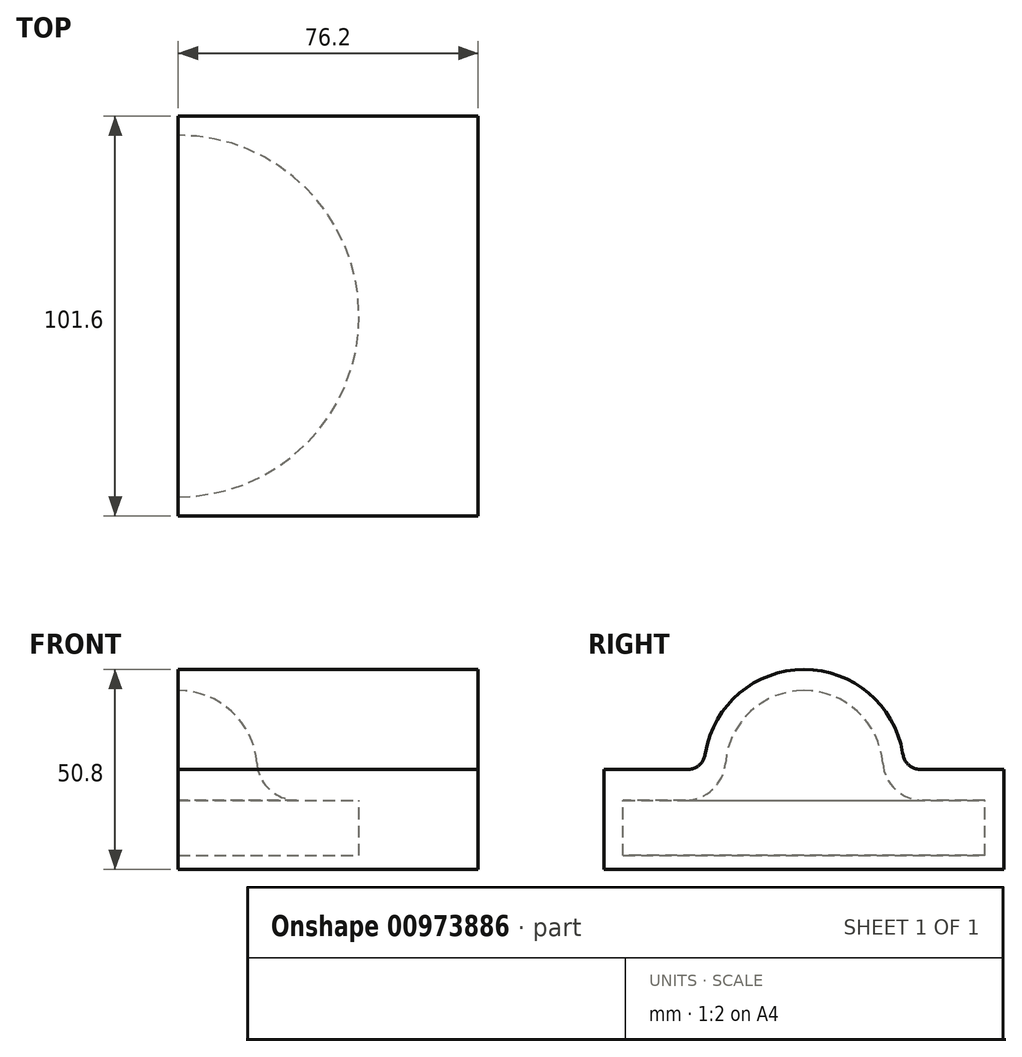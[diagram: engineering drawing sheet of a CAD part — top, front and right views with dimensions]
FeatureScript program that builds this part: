
annotation { "Feature Type Name" : "Feature", "Feature Type Description" : "" }
export const myFeature = defineFeature(function(context is Context, id is Id, definition is map)
    precondition{}
    {
        {
            var Q0;
            Q0=qCreatedBy(makeId("Right.planeOp"),FACE);
            var sketch = newSketch(context, id + "F0", { "sketchPlane" : qUnion([Q0])});
            skLineSegment(sketch, "E0.bottom", {"start": v(0, 0) * mm, "end": v(50.8, 0) * mm});
            skLineSegment(sketch, "E0.top", {"start": v(25.4, 25.4) * mm, "end": v(50.8, 25.4) * mm});
            skLineSegment(sketch, "E0.left", {"start": v(0, 0) * mm, "end": v(0, 25.4) * mm, "construction": true});
            skLineSegment(sketch, "E0.right", {"start": v(50.8, 0) * mm, "end": v(50.8, 25.4) * mm});
            skLineSegment(sketch, "E1.MirrorCS", {"start": v(-25.4, 25.4) * mm, "end": v(-50.8, 25.4) * mm});
            skLineSegment(sketch, "E2.MirrorCS", {"start": v(-50.8, 0) * mm, "end": v(-50.8, 25.4) * mm});
            skLineSegment(sketch, "E3.MirrorCS", {"start": v(0, 0) * mm, "end": v(-50.8, 0) * mm});
            skArc(sketch, "E4", {"start": v(-25.4, 25.4) * mm, "mid": v(0, 50.8) * mm, "end": v(25.4, 25.4) * mm});
            skLineSegment(sketch, "E5", {"start": v(0, 50.8) * mm, "end": v(0, 25.4) * mm, "construction": true});
            skSolve(sketch);
        }
        {
            var Q0;
            Q0=makeQuery(id+"F0.imprint","IMPRINT",FACE,{"disambiguationData":[TD([[makeQuery(id+"F0.imprint","IMPRINT",EDGE,{"derivedFrom":sQuery(id+"F0.wireOp",EDGE,"E0.bottom")}),1.0]])]});
            extrude(context, id + "F1", {"entities" : qUnion([Q0]), "depth" : 76.2 * mm, "offsetDistance" : 25.4 * mm});
        }
        {
            var Q0;
            Q0=makeQuery(id+"F1.opExtrude","SWEPT_EDGE",EDGE,{"disambiguationData":[OSD([sQuery(id+"F0.wireOp",EDGE,"E1.MirrorCS"),sQuery(id+"F0.wireOp",EDGE,"E4")])]});
            var Q1;
            Q1=makeQuery(id+"F1.opExtrude","SWEPT_EDGE",EDGE,{"disambiguationData":[OSD([sQuery(id+"F0.wireOp",EDGE,"E0.top"),sQuery(id+"F0.wireOp",EDGE,"E4")])]});
            fillet(context, id + "F2", {"entities" : qUnion([Q0, Q1]), "radius" : 5.08 * mm, "tangentPropagation" : true, "rho" : 0.5, "crossSection" : FilletCrossSection.CONIC, "allowEdgeOverflow" : false});
        }
        {
            var Q0;
            Q0=makeQuery(id+"F1.opExtrude","CAP_FACE",FACE,{"disambiguationData":[OSD([sQuery(id+"F0.wireOp",EDGE,"E0.bottom"),sQuery(id+"F0.wireOp",EDGE,"E0.top"),sQuery(id+"F0.wireOp",EDGE,"E0.right"),sQuery(id+"F0.wireOp",EDGE,"E1.MirrorCS"),sQuery(id+"F0.wireOp",EDGE,"E2.MirrorCS"),sQuery(id+"F0.wireOp",EDGE,"E3.MirrorCS"),sQuery(id+"F0.wireOp",EDGE,"E4")])],"isStart":true});
            var sketch = newSketch(context, id + "F3", { "sketchPlane" : qUnion([Q0])});
            skLineSegment(sketch, "E6.top", {"start": v(0, 3.5) * mm, "end": v(45.94, 3.5) * mm});
            skLineSegment(sketch, "E6.right", {"start": v(45.94, 17.6) * mm, "end": v(45.94, 3.5) * mm});
            skLineSegment(sketch, "E7.trimOffspring", {"start": v(18.46, 17.6) * mm, "end": v(45.94, 17.6) * mm});
            skArc(sketch, "E8.trimOffspring", {"start": v(18.46, 17.6) * mm, "mid": v(16.7, 36.47) * mm, "end": v(0, 45.44) * mm});
            skLineSegment(sketch, "E9", {"start": v(0, 45.44) * mm, "end": v(0, 3.5) * mm});
            skSolve(sketch);
        }
        {
            var Q0;
            Q0 = qSketchRegion(id + "F3", true);
            var Q1;
            Q1=sQuery(id+"F3.wireOp",EDGE,"E9");
            revolve(context, id + "F4", {"operationType" : NewBodyOperationType.REMOVE, "surfaceOperationType" : NewSurfaceOperationType.NEW, "entities" : qUnion([Q0]), "axis" : qUnion([Q1]), "revolveType" : RevolveType.FULL});
        }
        {
            var Q0;
            Q0=makeQuery(id+"F4.boolean.opBoolean","COPY",EDGE,{"derivedFrom":makeQuery(id+"F4.opRevolve","SWEPT_EDGE",EDGE,{"disambiguationData":[OSD([sQuery(id+"F3.wireOp",EDGE,"E7.trimOffspring"),sQuery(id+"F3.wireOp",EDGE,"E8.trimOffspring")])]})});
            fillet(context, id + "F5", {"entities" : qUnion([Q0]), "radius" : 10.16 * mm, "tangentPropagation" : true, "allowEdgeOverflow" : false});
        }
    });
